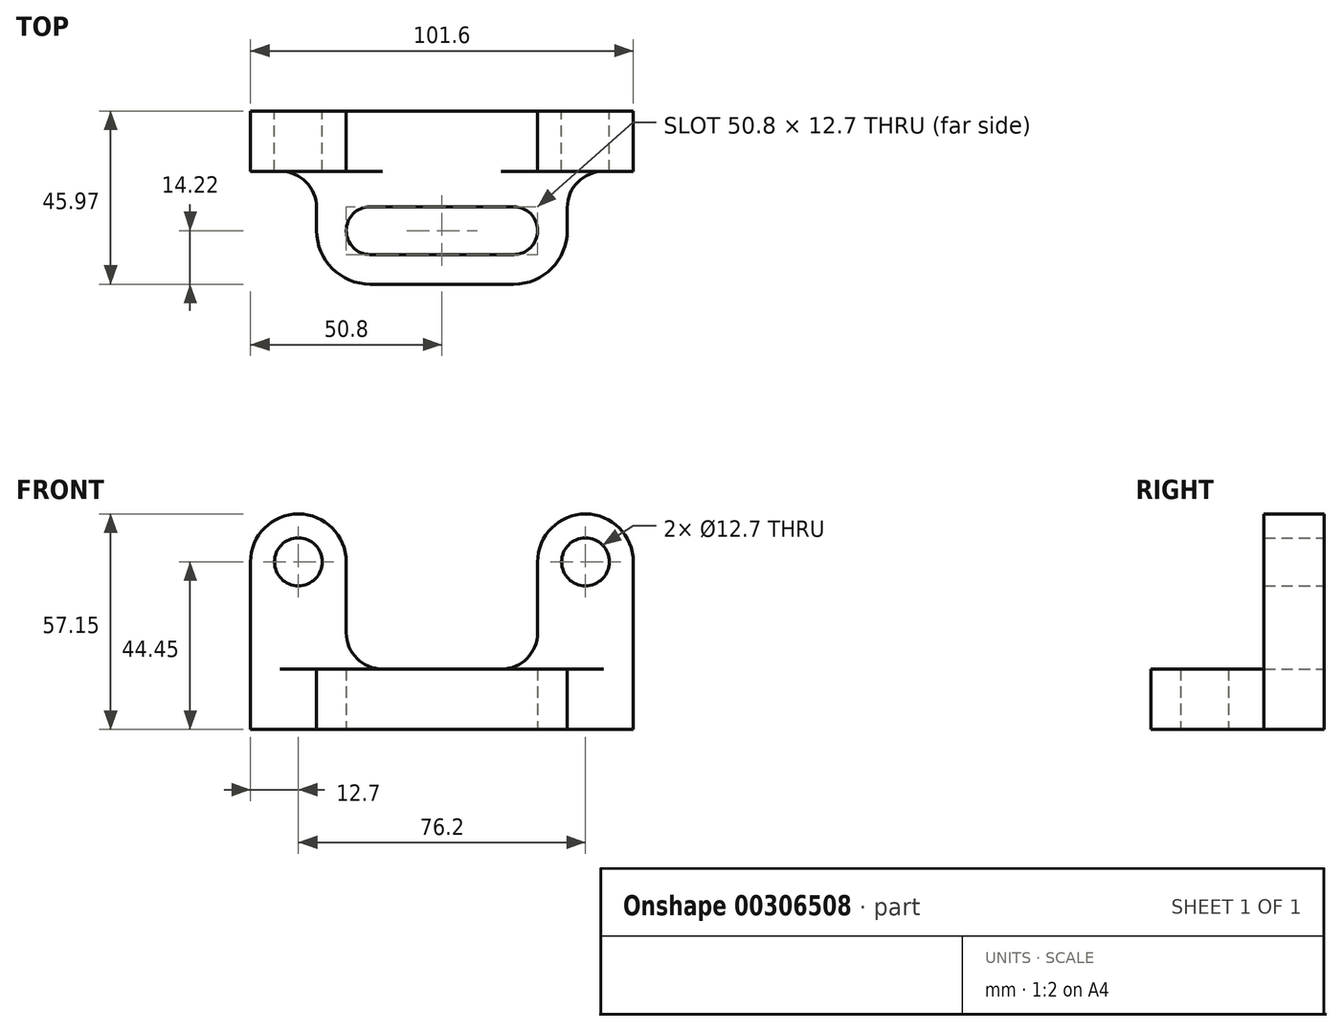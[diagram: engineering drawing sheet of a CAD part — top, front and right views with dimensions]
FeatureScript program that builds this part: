
annotation { "Feature Type Name" : "Feature", "Feature Type Description" : "" }
export const myFeature = defineFeature(function(context is Context, id is Id, definition is map)
    precondition{}
    {
        {
            var Q0;
            Q0=qCreatedBy(makeId("Front.planeOp"),FACE);
            var sketch = newSketch(context, id + "F0", { "sketchPlane" : qUnion([Q0])});
            skLineSegment(sketch, "E0", {"start": v(0, 0) * mm, "end": v(0, 44.45) * mm});
            skLineSegment(sketch, "E1", {"start": v(25.4, 44.45) * mm, "end": v(25.4, 25.65) * mm});
            skLineSegment(sketch, "E2", {"start": v(35.05, 16) * mm, "end": v(66.55, 16) * mm});
            skLineSegment(sketch, "E3", {"start": v(76.2, 25.65) * mm, "end": v(76.2, 44.45) * mm});
            skLineSegment(sketch, "E4", {"start": v(101.6, 44.45) * mm, "end": v(101.6, 0) * mm});
            skLineSegment(sketch, "E5", {"start": v(101.6, 0) * mm, "end": v(0, 0) * mm});
            skCircle(sketch, "E6", {"center": v(12.7, 44.45) * mm, "radius": 6.35 * mm});
            skArc(sketch, "E7", {"start": v(25.4, 44.45) * mm, "mid": v(12.7, 57.15) * mm, "end": v(0, 44.45) * mm});
            skCircle(sketch, "E8", {"center": v(88.9, 44.45) * mm, "radius": 6.35 * mm});
            skArc(sketch, "E9", {"start": v(101.6, 44.45) * mm, "mid": v(88.9, 57.15) * mm, "end": v(76.2, 44.45) * mm});
            skArc(sketch, "E10", {"start": v(25.4, 25.65) * mm, "mid": v(28.23, 18.83) * mm, "end": v(35.05, 16) * mm});
            skArc(sketch, "E11", {"start": v(66.55, 16) * mm, "mid": v(73.37, 18.83) * mm, "end": v(76.2, 25.65) * mm});
            skPoint(sketch, "E12.endSnap0", {"position": v(50.8, 16) * mm});
            skSolve(sketch);
        }
        {
            var Q0;
            Q0=makeQuery(id+"F0.imprint","IMPRINT",FACE,{"disambiguationData":[TD([[makeQuery(id+"F0.imprint","IMPRINT",EDGE,{"derivedFrom":sQuery(id+"F0.wireOp",EDGE,"E0")}),-1.0]])]});
            extrude(context, id + "F1", {"entities" : qUnion([Q0]), "depth" : 16 * mm});
        }
        {
            var Q0;
            Q0=makeQuery(id+"F1.opExtrude","CAP_FACE",FACE,{"disambiguationData":[OSD([sQuery(id+"F0.wireOp",EDGE,"E0"),sQuery(id+"F0.wireOp",EDGE,"E1"),sQuery(id+"F0.wireOp",EDGE,"E2"),sQuery(id+"F0.wireOp",EDGE,"E3"),sQuery(id+"F0.wireOp",EDGE,"E4"),sQuery(id+"F0.wireOp",EDGE,"E5"),sQuery(id+"F0.wireOp",EDGE,"E6"),sQuery(id+"F0.wireOp",EDGE,"E7"),sQuery(id+"F0.wireOp",EDGE,"E8"),sQuery(id+"F0.wireOp",EDGE,"E9"),sQuery(id+"F0.wireOp",EDGE,"E10"),sQuery(id+"F0.wireOp",EDGE,"E11")])],"isStart":false});
            var sketch = newSketch(context, id + "F2", { "sketchPlane" : qUnion([Q0])});
            skPoint(sketch, "E13.oppositeSnap0", {"position": v(50.8, 16) * mm});
            skLineSegment(sketch, "E13.bottom", {"start": v(0, 0) * mm, "end": v(101.6, 0) * mm});
            skLineSegment(sketch, "E13.top", {"start": v(0, 16) * mm, "end": v(101.6, 16) * mm});
            skLineSegment(sketch, "E13.left", {"start": v(0, 0) * mm, "end": v(0, 16) * mm});
            skLineSegment(sketch, "E13.right", {"start": v(101.6, 0) * mm, "end": v(101.6, 16) * mm});
            skSolve(sketch);
        }
        {
            var Q0;
            Q0=makeQuery(id+"F2.imprint","IMPRINT",FACE,{"disambiguationData":[TD([[makeQuery(id+"F2.imprint","IMPRINT",EDGE,{"derivedFrom":sQuery(id+"F2.wireOp",EDGE,"E13.bottom")}),-1.0]])]});
            extrude(context, id + "F3", {"entities" : qUnion([Q0]), "operationType" : NewBodyOperationType.ADD, "depth" : 29.97 * mm});
        }
        {
            var Q0;
            Q0=makeQuery(id+"F3.boolean.opBoolean","MERGE",FACE,{"derivedFrom":[makeQuery(id+"F1.opExtrude","SWEPT_FACE",FACE,{"disambiguationData":[OSD([sQuery(id+"F0.wireOp",EDGE,"E5")])]}),makeQuery(id+"F3.opExtrude","SWEPT_FACE",FACE,{"disambiguationData":[OSD([sQuery(id+"F2.wireOp",EDGE,"E13.bottom")])]})]});
            var sketch = newSketch(context, id + "F4", { "sketchPlane" : qUnion([Q0])});
            skLineSegment(sketch, "E14", {"start": v(0.14, 31.75) * mm, "end": v(105.12, 31.75) * mm, "construction": true});
            skArc(sketch, "E15", {"start": v(31.75, 38.1) * mm, "mid": v(25.4, 31.75) * mm, "end": v(31.75, 25.4) * mm});
            skArc(sketch, "E16", {"start": v(69.85, 25.4) * mm, "mid": v(76.2, 31.75) * mm, "end": v(69.85, 38.1) * mm});
            skArc(sketch, "E17", {"start": v(31.75, 45.97) * mm, "mid": v(21.7, 41.8) * mm, "end": v(17.53, 31.75) * mm});
            skArc(sketch, "E18", {"start": v(84.07, 31.75) * mm, "mid": v(79.9, 41.8) * mm, "end": v(69.85, 45.97) * mm});
            skLineSegment(sketch, "E19", {"start": v(31.75, 45.97) * mm, "end": v(69.85, 45.97) * mm});
            skLineSegment(sketch, "E20", {"start": v(31.75, 38.1) * mm, "end": v(69.85, 38.1) * mm});
            skLineSegment(sketch, "E21", {"start": v(31.75, 25.4) * mm, "end": v(69.85, 25.4) * mm});
            skLineSegment(sketch, "E22", {"start": v(0, 16) * mm, "end": v(7.87, 16) * mm});
            skArc(sketch, "E23", {"start": v(7.87, 16) * mm, "mid": v(14.7, 18.83) * mm, "end": v(17.53, 25.65) * mm});
            skLineSegment(sketch, "E24", {"start": v(17.53, 25.65) * mm, "end": v(17.53, 31.75) * mm});
            skArc(sketch, "E25", {"start": v(84.07, 25.65) * mm, "mid": v(86.9, 18.83) * mm, "end": v(93.73, 16) * mm});
            skLineSegment(sketch, "E26", {"start": v(84.07, 25.65) * mm, "end": v(84.07, 31.75) * mm});
            skLineSegment(sketch, "E27.trimOffspring", {"start": v(93.73, 16) * mm, "end": v(101.6, 16) * mm});
            skSolve(sketch);
        }
        {
            var Q0;
            {var subQ1=sQuery(id+"F4.wireOp",EDGE,"E17");Q0=makeQuery(id+"F4.imprint","IMPRINT",FACE,{"disambiguationData":[TD([[makeQuery(id+"F4.imprint","IMPRINT",EDGE,{"derivedFrom":subQ1}),-1.0]])]});}
            var Q1;
            {var subQ1=sQuery(id+"F4.wireOp",EDGE,"E18");Q1=makeQuery(id+"F4.imprint","IMPRINT",FACE,{"disambiguationData":[TD([[makeQuery(id+"F4.imprint","IMPRINT",EDGE,{"derivedFrom":subQ1}),-1.0]])]});}
            var Q2;
            Q2=makeQuery(id+"F4.imprint","IMPRINT",FACE,{"disambiguationData":[TD([[makeQuery(id+"F4.imprint","IMPRINT",EDGE,{"derivedFrom":sQuery(id+"F4.wireOp",EDGE,"E15")}),1.0]])]});
            extrude(context, id + "F5", {"entities" : qUnion([Q0, Q1, Q2]), "operationType" : NewBodyOperationType.REMOVE, "endBound" : BoundingType.THROUGH_ALL, "oppositeDirection" : true, "depth" : 25.4 * mm});
        }
    });
